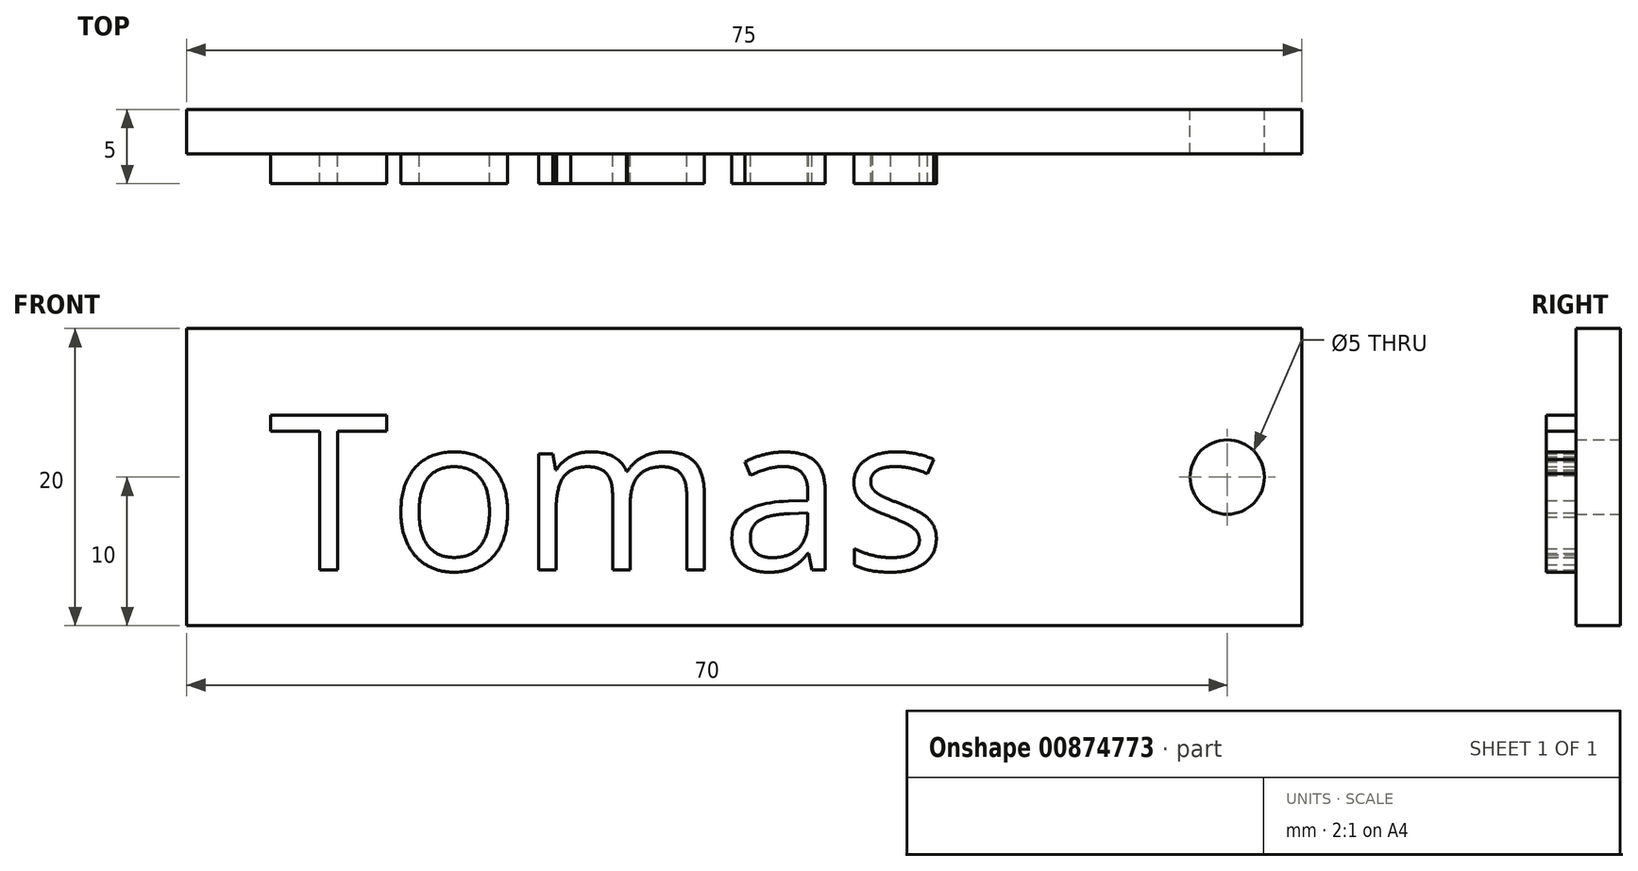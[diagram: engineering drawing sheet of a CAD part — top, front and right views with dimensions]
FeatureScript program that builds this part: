
annotation { "Feature Type Name" : "Feature", "Feature Type Description" : "" }
export const myFeature = defineFeature(function(context is Context, id is Id, definition is map)
    precondition{}
    {
        {
            var Q0;
            Q0=qCreatedBy(makeId("Front.planeOp"),FACE);
            var sketch = newSketch(context, id + "F0", { "sketchPlane" : qUnion([Q0])});
            skLineSegment(sketch, "E0.bottom", {"start": v(0, 0) * mm, "end": v(75, 0) * mm});
            skLineSegment(sketch, "E0.top", {"start": v(0, -20) * mm, "end": v(75, -20) * mm});
            skLineSegment(sketch, "E0.left", {"start": v(0, 0) * mm, "end": v(0, -20) * mm});
            skLineSegment(sketch, "E0.right", {"start": v(75, 0) * mm, "end": v(75, -20) * mm});
            skCircle(sketch, "E1", {"center": v(70, -10) * mm, "radius": 2.5 * mm});
            skSolve(sketch);
        }
        {
            var Q0;
            Q0=makeQuery(id+"F0.imprint","IMPRINT",FACE,{"disambiguationData":[TD([[makeQuery(id+"F0.imprint","IMPRINT",EDGE,{"derivedFrom":sQuery(id+"F0.wireOp",EDGE,"E0.bottom")}),-1.0]])]});
            extrude(context, id + "F1", {"entities" : qUnion([Q0]), "depth" : 3 * mm, "offsetDistance" : 25 * mm});
        }
        {
            var Q0;
            Q0=makeQuery(id+"F1.opExtrude","CAP_FACE",FACE,{"disambiguationData":[OSD([sQuery(id+"F0.wireOp",EDGE,"E0.bottom"),sQuery(id+"F0.wireOp",EDGE,"E0.top"),sQuery(id+"F0.wireOp",EDGE,"E0.left"),sQuery(id+"F0.wireOp",EDGE,"E0.right"),sQuery(id+"F0.wireOp",EDGE,"E1")])],"isStart":false});
            var sketch = newSketch(context, id + "F2", { "sketchPlane" : qUnion([Q0])});
            skText(sketch, "E2", { "text": "Tomas", "fontName": "OpenSans-Regular.ttf"});
            const initialGuessF2  = {"E2": [0.0055, -0.01626, 1, 0, 0.01052]};
            skSetInitialGuess(sketch, initialGuessF2);
            skSolve(sketch);
        }
        {
            var Q0;
            Q0 = qSketchRegion(id + "F2", true);
            extrude(context, id + "F3", {"entities" : qUnion([Q0]), "operationType" : NewBodyOperationType.ADD, "depth" : 2 * mm, "offsetDistance" : 25 * mm});
        }
    });
